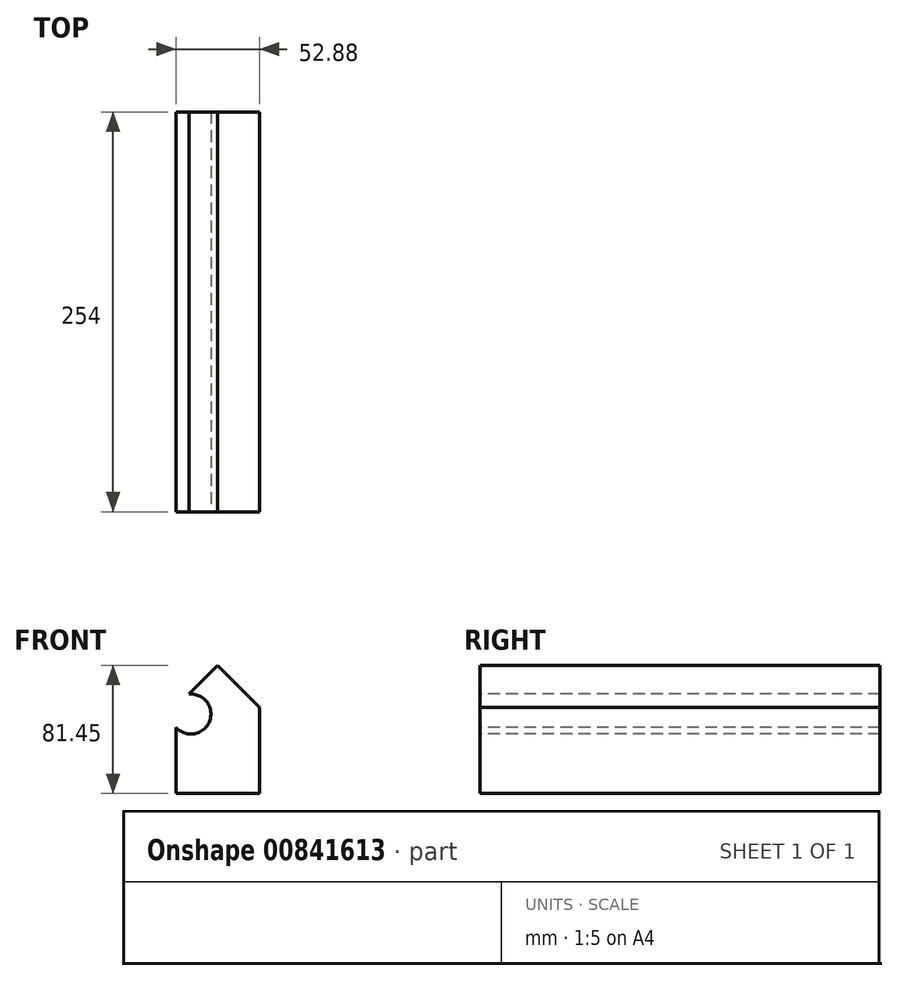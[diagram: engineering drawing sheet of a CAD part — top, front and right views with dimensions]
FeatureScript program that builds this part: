
annotation { "Feature Type Name" : "Feature", "Feature Type Description" : "" }
export const myFeature = defineFeature(function(context is Context, id is Id, definition is map)
    precondition{}
    {
        {
            var Q0;
            Q0=qCreatedBy(makeId("Front.planeOp"),FACE);
            var sketch = newSketch(context, id + "F0", { "sketchPlane" : qUnion([Q0])});
            skLineSegment(sketch, "E0", {"start": v(-26.43, 23.13) * mm, "end": v(-26.43, -31.6) * mm});
            skLineSegment(sketch, "E1", {"start": v(-26.43, -31.6) * mm, "end": v(26.45, -31.6) * mm});
            skLineSegment(sketch, "E2", {"start": v(-26.43, 23.13) * mm, "end": v(0, 49.85) * mm});
            skLineSegment(sketch, "E3", {"start": v(26.45, -31.6) * mm, "end": v(26.45, 23.13) * mm});
            skLineSegment(sketch, "E4", {"start": v(26.45, 23.13) * mm, "end": v(0, 49.85) * mm});
            skSolve(sketch);
        }
        {
            var Q0;
            Q0=makeQuery(id+"F0.imprint","IMPRINT",FACE,{"disambiguationData":[TD([[makeQuery(id+"F0.imprint","IMPRINT",EDGE,{"derivedFrom":sQuery(id+"F0.wireOp",EDGE,"E0")}),1.0]])]});
            extrude(context, id + "F1", {"entities" : qUnion([Q0]), "depth" : 254 * mm, "offsetDistance" : 25.4 * mm});
        }
        {
            var Q0;
            Q0=makeQuery(id+"F1.opExtrude","CAP_FACE",FACE,{"disambiguationData":[OSD([sQuery(id+"F0.wireOp",EDGE,"E0"),sQuery(id+"F0.wireOp",EDGE,"E1"),sQuery(id+"F0.wireOp",EDGE,"E2"),sQuery(id+"F0.wireOp",EDGE,"E3"),sQuery(id+"F0.wireOp",EDGE,"E4")])],"isStart":false});
            var sketch = newSketch(context, id + "F2", { "sketchPlane" : qUnion([Q0])});
            skCircle(sketch, "E5", {"center": v(-17, 18.93) * mm, "radius": 7.4 * mm});
            skSolve(sketch);
        }
        {
            var Q0;
            Q0=sQuery(id+"F2.wireOp",VERTEX,"E5.center");
            var Q1;
            Q1=makeQuery(id+"F1.opExtrude","SWEPT_BODY",BODY,{"disambiguationData":[OSD([sQuery(id+"F0.wireOp",EDGE,"E0"),sQuery(id+"F0.wireOp",EDGE,"E1"),sQuery(id+"F0.wireOp",EDGE,"E2"),sQuery(id+"F0.wireOp",EDGE,"E3"),sQuery(id+"F0.wireOp",EDGE,"E4")])]});
            hole(context, id + "F3", {"style" : HoleStyle.SIMPLE, "endStyle" : HoleEndStyle.THROUGH, "holeDiameter" : 25.4 * mm, "majorDiameter" : 6.35 * mm, "isTappedThrough" : true, "tappedDepth" : 12.7 * mm, "tapClearance" : 3, "locations" : qUnion([Q0]), "scope" : qUnion([Q1])});
        }
    });
